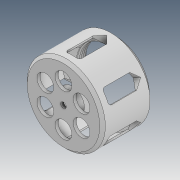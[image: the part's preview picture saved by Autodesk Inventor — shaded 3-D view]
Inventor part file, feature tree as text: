
AUTODESK INVENTOR PART (.ipt)
format: ipt  version: 2020 (Build 240168000, 168)  size: 484,864 bytes
history: native  units: mm
features: sketch x9, extrude x8, chamfer x5, pattern_circular x2, helix x1, fillet x1, thicken_offset x1
ambient origin geometry x8: Origin, YZ Plane, XZ Plane, XY Plane, X Axis, Y Axis, Z Axis, Center Point
bodies: Solid1 (feature_tree)
feature tree (27):
  extrude  "Extrusion1"  Depth=1.6mm
  helix  "Coil1"  [1 undecoded]
  chamfer  "Chamfer1"  Distance=2.0mm Angle=45.0deg
  extrude  "Extrusion2"  Depth=36.0mm
  chamfer  "Chamfer2"  Distance=3.0mm
  extrude  "Extrusion3"  Depth=2.0mm
  extrude  "Extrusion4"  Depth=10.0mm
  chamfer  "Chamfer3"  Distance=12.0mm
  extrude  "Extrusion5"  Depth=10.0mm TaperAngle=360.0deg
  chamfer  "Chamfer4"  Distance=1.2mm
  extrude  "Extrusion6"  Depth=2.0mm TaperAngle=45.0deg
  chamfer  "Chamfer5"  Distance=16.0mm
  fillet  "Fillet1"  Radius=0.8mm
  pattern_circular  "Circular Pattern1"  [2 undecoded]
  extrude  "Extrusion7"  Depth=2.0mm TaperAngle=45.0deg
  thicken_offset  "Thicken1"
  extrude  "Extrusion8"  Depth=10.0mm
  pattern_circular  "Circular Pattern2"  [2 undecoded]
  sketch  "Sketch1"  dims[d0=43.9mm d1=1.6mm d2=7.0mm d3=0.0mm]
  sketch  "Sketch2"  dims[d4=1.2mm]
  sketch  "Sketch3"  dims[d5=0.8mm]
  sketch  "Sketch4"  dims[d6=1.5mm]
  sketch  "Sketch5"  dims[d7=5.8mm d8=10.0mm d9=0.0mm d10=90.0deg d11=90.0deg d12=0.0mm d13=0.0mm d14=0.475mm d15=2.0mm d16=45.0deg]
  sketch  "Sketch6"  dims[d17=56.0mm d18=36.0mm]
  sketch  "Sketch7"  dims[d19=1.2mm d20=3.0mm d21=0.0mm]
  sketch  "Sketch8"  dims[d22=1.45mm d23=2.0mm d24=45.0deg d25=1.2mm]
  sketch  "Sketch9"  dims[d26=30.0mm d27=0.0mm d28=15.0mm d29=12.0mm d30=60.0mm d32=360.0deg d34=1.2mm d35=0.0mm d36=4.85mm d37=2.0mm d38=45.0deg d39=16.0mm d40=0.8mm d41=4.0mm d42=0.0mm d43=1.0mm d44=2.0mm d45=45.0deg d46=10.0mm d47=10.0mm d48=0.0mm d49=5.0mm d50=2.0mm d51=45.0deg d52=2.0mm d53=60.0mm d54=360.0deg d56=4.0mm d57=10.0mm d58=0.0mm d59=1.0mm d60=1.0mm d61=3.0mm d62=2.96706mm d63=0.523599mm d64=1.2mm d65=5.0mm d66=0.0mm d67=30.0mm d68=360.0deg]
note: 5 required parameter values undecoded (feature->parameter linkage not recoverable at this tier; creation-order binding heuristic only, values carry confidence <= 0.55)
